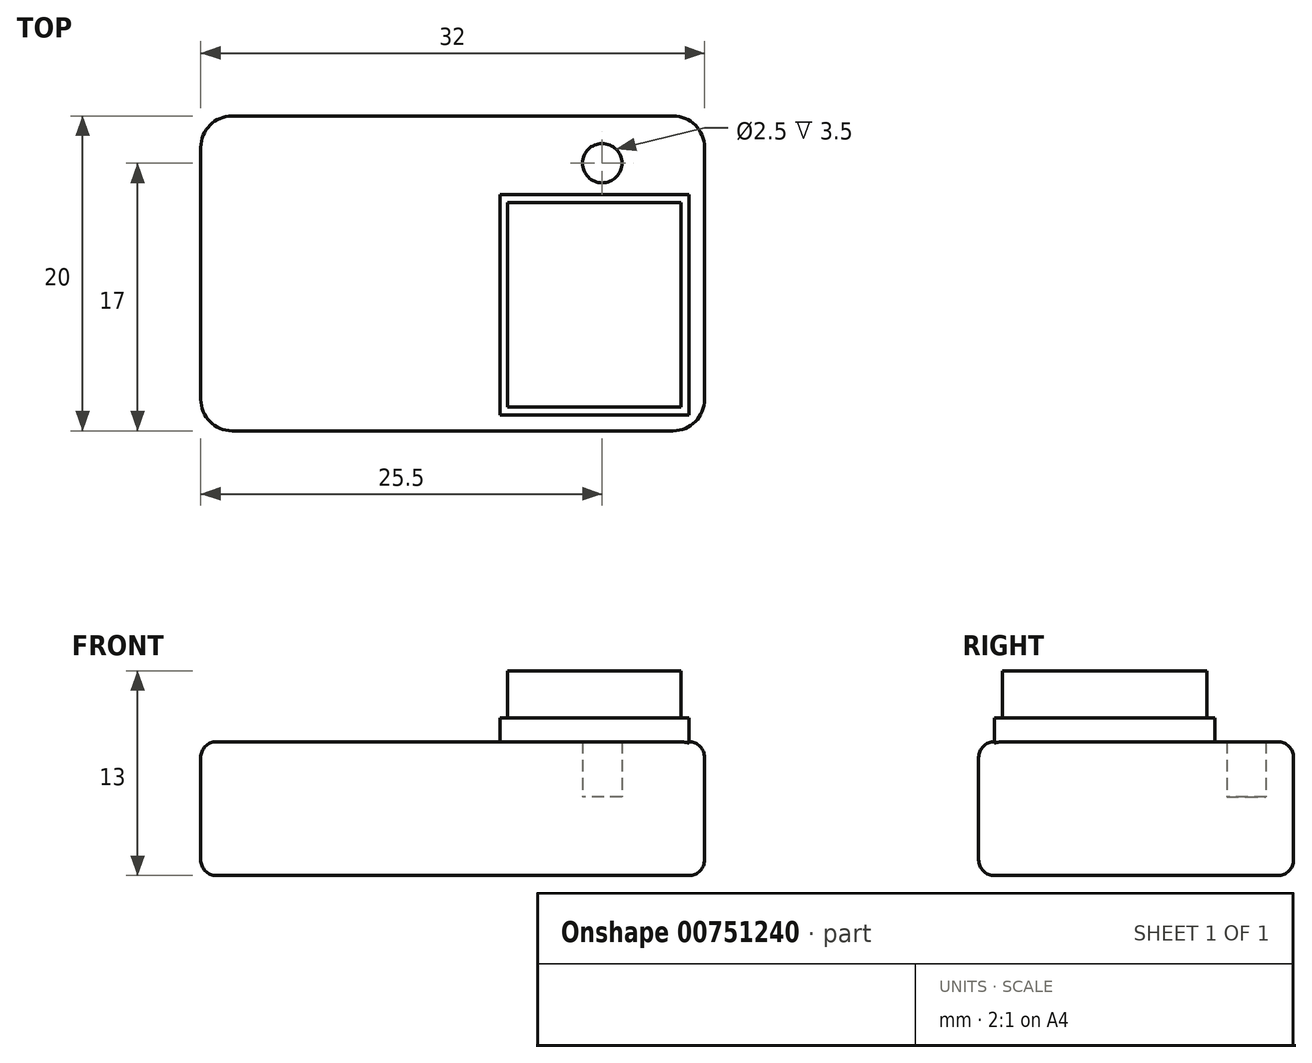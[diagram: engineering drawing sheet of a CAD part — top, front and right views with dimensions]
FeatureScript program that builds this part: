
annotation { "Feature Type Name" : "Feature", "Feature Type Description" : "" }
export const myFeature = defineFeature(function(context is Context, id is Id, definition is map)
    precondition{}
    {
        {
            var Q0;
            Q0=qCreatedBy(makeId("Top.planeOp"),FACE);
            var sketch = newSketch(context, id + "F0", { "sketchPlane" : qUnion([Q0])});
            skLineSegment(sketch, "E0.bottom", {"start": v(-16, 10) * mm, "end": v(16, 10) * mm});
            skLineSegment(sketch, "E0.top", {"start": v(-16, -10) * mm, "end": v(16, -10) * mm});
            skLineSegment(sketch, "E0.left", {"start": v(-16, 10) * mm, "end": v(-16, -10) * mm});
            skLineSegment(sketch, "E0.right", {"start": v(16, 10) * mm, "end": v(16, -10) * mm});
            skPoint(sketch, "E0.middle", {"position": v(0, 0) * mm});
            skLineSegment(sketch, "E1.bottom", {"start": v(14.5, -8.5) * mm, "end": v(3.5, -8.5) * mm});
            skLineSegment(sketch, "E1.top", {"start": v(14.5, 4.5) * mm, "end": v(3.5, 4.5) * mm});
            skLineSegment(sketch, "E1.left", {"start": v(14.5, -8.5) * mm, "end": v(14.5, 4.5) * mm});
            skLineSegment(sketch, "E1.right", {"start": v(3.5, -8.5) * mm, "end": v(3.5, 4.5) * mm});
            skLineSegment(sketch, "E2.bottom", {"start": v(15, -9) * mm, "end": v(3, -9) * mm});
            skLineSegment(sketch, "E2.top", {"start": v(15, 5) * mm, "end": v(3, 5) * mm});
            skLineSegment(sketch, "E2.left", {"start": v(15, -9) * mm, "end": v(15, 5) * mm});
            skLineSegment(sketch, "E2.right", {"start": v(3, -9) * mm, "end": v(3, 5) * mm});
            skLineSegment(sketch, "E3", {"start": v(9, 4.5) * mm, "end": v(9, 5) * mm, "construction": true});
            skLineSegment(sketch, "E4", {"start": v(3.5, -2) * mm, "end": v(3, -2) * mm, "construction": true});
            skLineSegment(sketch, "E5", {"start": v(9, -8.5) * mm, "end": v(9, -9) * mm, "construction": true});
            skLineSegment(sketch, "E6", {"start": v(14.5, -2) * mm, "end": v(15, -2) * mm, "construction": true});
            skCircle(sketch, "E7", {"center": v(9.5, 7) * mm, "radius": 1.25 * mm});
            skSolve(sketch);
        }
        {
            var Q0;
            Q0=makeQuery(id+"F0.imprint","IMPRINT",FACE,{"disambiguationData":[TD([[makeQuery(id+"F0.imprint","IMPRINT",EDGE,{"derivedFrom":sQuery(id+"F0.wireOp",EDGE,"E0.bottom")}),-1.0]])]});
            var Q1;
            Q1=makeQuery(id+"F0.imprint","IMPRINT",FACE,{"disambiguationData":[TD([[makeQuery(id+"F0.imprint","IMPRINT",EDGE,{"derivedFrom":sQuery(id+"F0.wireOp",EDGE,"E1.bottom")}),1.0]])]});
            var Q2;
            Q2=makeQuery(id+"F0.imprint","IMPRINT",FACE,{"disambiguationData":[TD([[makeQuery(id+"F0.imprint","IMPRINT",EDGE,{"derivedFrom":sQuery(id+"F0.wireOp",EDGE,"E1.bottom")}),-1.0]])]});
            extrude(context, id + "F1", {"entities" : qUnion([Q0, Q1, Q2]), "depth" : 8.5 * mm, "offsetDistance" : 25 * mm});
        }
        {
            var Q0;
            Q0=makeQuery(id+"F0.imprint","IMPRINT",FACE,{"disambiguationData":[TD([[makeQuery(id+"F0.imprint","IMPRINT",EDGE,{"derivedFrom":sQuery(id+"F0.wireOp",EDGE,"E7")}),1.0]])]});
            extrude(context, id + "F2", {"entities" : qUnion([Q0]), "operationType" : NewBodyOperationType.ADD, "depth" : 5 * mm, "offsetDistance" : 25 * mm});
        }
        {
            var Q0;
            Q0=makeQuery(id+"F1.opExtrude","SWEPT_EDGE",EDGE,{"disambiguationData":[OSD([sQuery(id+"F0.wireOp",EDGE,"E0.bottom"),sQuery(id+"F0.wireOp",EDGE,"E0.left")])]});
            var Q1;
            Q1=makeQuery(id+"F1.opExtrude","SWEPT_EDGE",EDGE,{"disambiguationData":[OSD([sQuery(id+"F0.wireOp",EDGE,"E0.top"),sQuery(id+"F0.wireOp",EDGE,"E0.left")])]});
            var Q2;
            Q2=makeQuery(id+"F1.opExtrude","SWEPT_EDGE",EDGE,{"disambiguationData":[OSD([sQuery(id+"F0.wireOp",EDGE,"E0.top"),sQuery(id+"F0.wireOp",EDGE,"E0.right")])]});
            var Q3;
            Q3=makeQuery(id+"F1.opExtrude","SWEPT_EDGE",EDGE,{"disambiguationData":[OSD([sQuery(id+"F0.wireOp",EDGE,"E0.bottom"),sQuery(id+"F0.wireOp",EDGE,"E0.right")])]});
            fillet(context, id + "F3", {"entities" : qUnion([Q0, Q1, Q2, Q3]), "radius" : 2 * mm, "tangentPropagation" : true, "allowEdgeOverflow" : false});
        }
        {
            var Q0;
            Q0=makeQuery(id+"F0.imprint","IMPRINT",FACE,{"disambiguationData":[TD([[makeQuery(id+"F0.imprint","IMPRINT",EDGE,{"derivedFrom":sQuery(id+"F0.wireOp",EDGE,"E1.bottom")}),-1.0]])]});
            extrude(context, id + "F4", {"entities" : qUnion([Q0]), "operationType" : NewBodyOperationType.ADD, "depth" : 13 * mm, "offsetDistance" : 25 * mm});
        }
        {
            var Q0;
            Q0=makeQuery(id+"F0.imprint","IMPRINT",FACE,{"disambiguationData":[TD([[makeQuery(id+"F0.imprint","IMPRINT",EDGE,{"derivedFrom":sQuery(id+"F0.wireOp",EDGE,"E1.bottom")}),1.0]])]});
            extrude(context, id + "F5", {"entities" : qUnion([Q0]), "operationType" : NewBodyOperationType.ADD, "depth" : 10 * mm, "offsetDistance" : 25 * mm});
        }
        {
            var Q0;
            Q0=makeQuery(id+"F1.opExtrude","SWEPT_FACE",FACE,{"disambiguationData":[OSD([sQuery(id+"F0.wireOp",EDGE,"E0.top")])]});
            fillet(context, id + "F6", {"entities" : qUnion([Q0]), "radius" : 1 * mm, "tangentPropagation" : true, "allowEdgeOverflow" : false});
        }
    });
